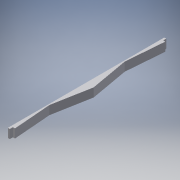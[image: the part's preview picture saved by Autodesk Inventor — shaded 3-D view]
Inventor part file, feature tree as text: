
AUTODESK INVENTOR PART (.ipt)
format: ipt  version: 2017 (Build 210142000, 142)  size: 121,344 bytes
history: native  units: in
note: dims shown in document units (in); Inventor stores cm internally (conversion verified against a paired STEP export)
features: extrude x3, sketch x3
ambient origin geometry x8: Origin, YZ Plane, XZ Plane, XY Plane, X Axis, Y Axis, Z Axis, Center Point
bodies: Solid1 (feature_tree)
feature tree (6):
  extrude  "Extrusion1"  Depth=0.134in
  sketch  "Sketch2"  dims[d2=0.134in d3=1.2285in]
  extrude  "Extrusion2"  Depth=0.134in
  extrude  "Extrusion3"  Depth=1.229in
  sketch  "Sketch1"  dims[d0=4.931in d1=0.134in]
  sketch  "Sketch3"  dims[d4=2.457in d5=1.229in d6=0.2875in d7=0.0in d8=0.065in d9=0.065in d10=0.101in d11=0.0in d12=0.101in d13=0.0in d15=0.259in d16=0.035in d17=0.035in]
